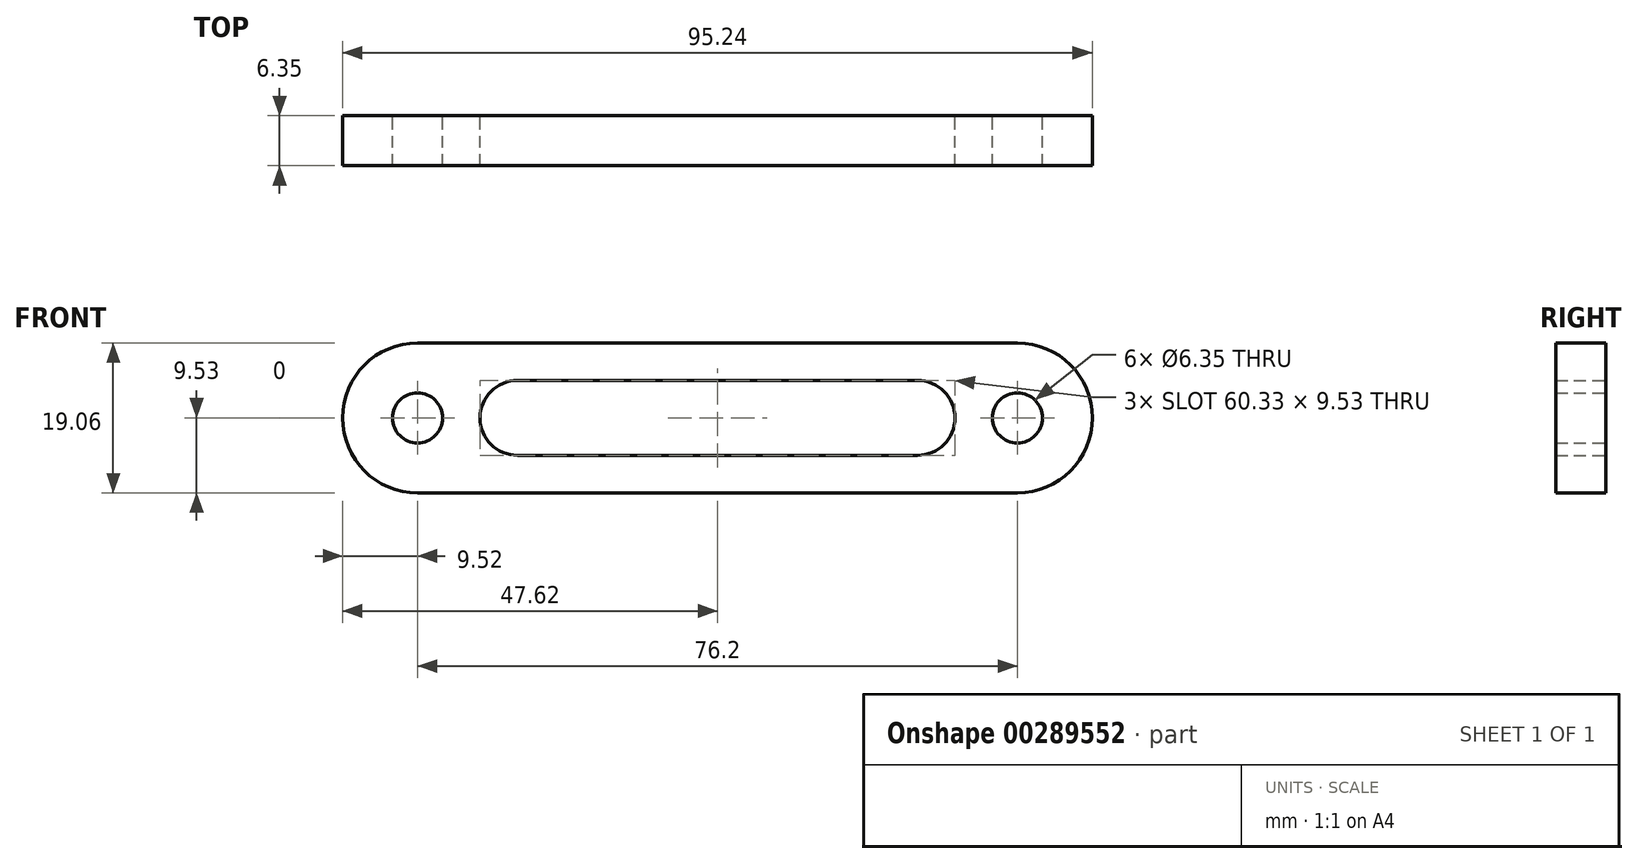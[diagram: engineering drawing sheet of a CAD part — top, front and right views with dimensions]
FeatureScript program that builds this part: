
annotation { "Feature Type Name" : "Feature", "Feature Type Description" : "" }
export const myFeature = defineFeature(function(context is Context, id is Id, definition is map)
    precondition{}
    {
        {
            var Q0;
            Q0=qCreatedBy(makeId("Front.planeOp"),FACE);
            var sketch = newSketch(context, id + "F0", { "sketchPlane" : qUnion([Q0])});
            skLineSegment(sketch, "E0.bottom", {"start": v(38.1, 9.53) * mm, "end": v(-38.1, 9.53) * mm});
            skLineSegment(sketch, "E0.top", {"start": v(38.1, -9.53) * mm, "end": v(-38.1, -9.53) * mm});
            skLineSegment(sketch, "E0.left", {"start": v(38.1, 9.52) * mm, "end": v(38.1, -9.53) * mm});
            skLineSegment(sketch, "E0.right", {"start": v(-38.1, 9.53) * mm, "end": v(-38.1, -9.53) * mm});
            skPoint(sketch, "E0.middle", {"position": v(0, 0) * mm});
            skCircle(sketch, "E1", {"center": v(-38.1, 0) * mm, "radius": 3.18 * mm});
            skLineSegment(sketch, "E2", {"start": v(0, 9.53) * mm, "end": v(0, -9.53) * mm, "construction": true});
            skCircle(sketch, "E3.MirrorC", {"center": v(38.1, 0) * mm, "radius": 3.18 * mm});
            skArc(sketch, "E4", {"start": v(38.1, -9.53) * mm, "mid": v(47.62, 0) * mm, "end": v(38.1, 9.52) * mm});
            skArc(sketch, "E5", {"start": v(-38.1, 9.53) * mm, "mid": v(-47.63, 0) * mm, "end": v(-38.1, -9.52) * mm});
            skLineSegment(sketch, "E6.bottom", {"start": v(25.4, 4.76) * mm, "end": v(-25.4, 4.76) * mm});
            skLineSegment(sketch, "E6.top", {"start": v(25.4, -4.76) * mm, "end": v(-25.4, -4.76) * mm});
            skLineSegment(sketch, "E6.left", {"start": v(25.4, 4.76) * mm, "end": v(25.4, -4.76) * mm});
            skLineSegment(sketch, "E6.right", {"start": v(-25.4, 4.76) * mm, "end": v(-25.4, -4.76) * mm});
            skArc(sketch, "E7", {"start": v(25.4, -4.76) * mm, "mid": v(30.16, 0) * mm, "end": v(25.4, 4.76) * mm});
            skArc(sketch, "E8", {"start": v(-25.4, 4.76) * mm, "mid": v(-30.16, 0) * mm, "end": v(-25.4, -4.76) * mm});
            skSolve(sketch);
        }
        {
            var Q0;
            {var subQ6=sQuery(id+"F0.wireOp",EDGE,"E0.bottom");Q0=makeQuery(id+"F0.imprint","IMPRINT",FACE,{"disambiguationData":[TD([[makeQuery(id+"F0.imprint","IMPRINT",EDGE,{"derivedFrom":subQ6}),1.0]])]});}
            var Q1;
            {var subQ0=sQuery(id+"F0.wireOp",EDGE,"E5");Q1=makeQuery(id+"F0.imprint","IMPRINT",FACE,{"disambiguationData":[TD([[makeQuery(id+"F0.imprint","IMPRINT",EDGE,{"derivedFrom":subQ0}),1.0]])]});}
            var Q2;
            {var subQ0=sQuery(id+"F0.wireOp",EDGE,"E4");Q2=makeQuery(id+"F0.imprint","IMPRINT",FACE,{"disambiguationData":[TD([[makeQuery(id+"F0.imprint","IMPRINT",EDGE,{"derivedFrom":subQ0}),1.0]])]});}
            extrude(context, id + "F1", {"entities" : qUnion([Q0, Q1, Q2]), "depth" : 6.35 * mm});
        }
    });
